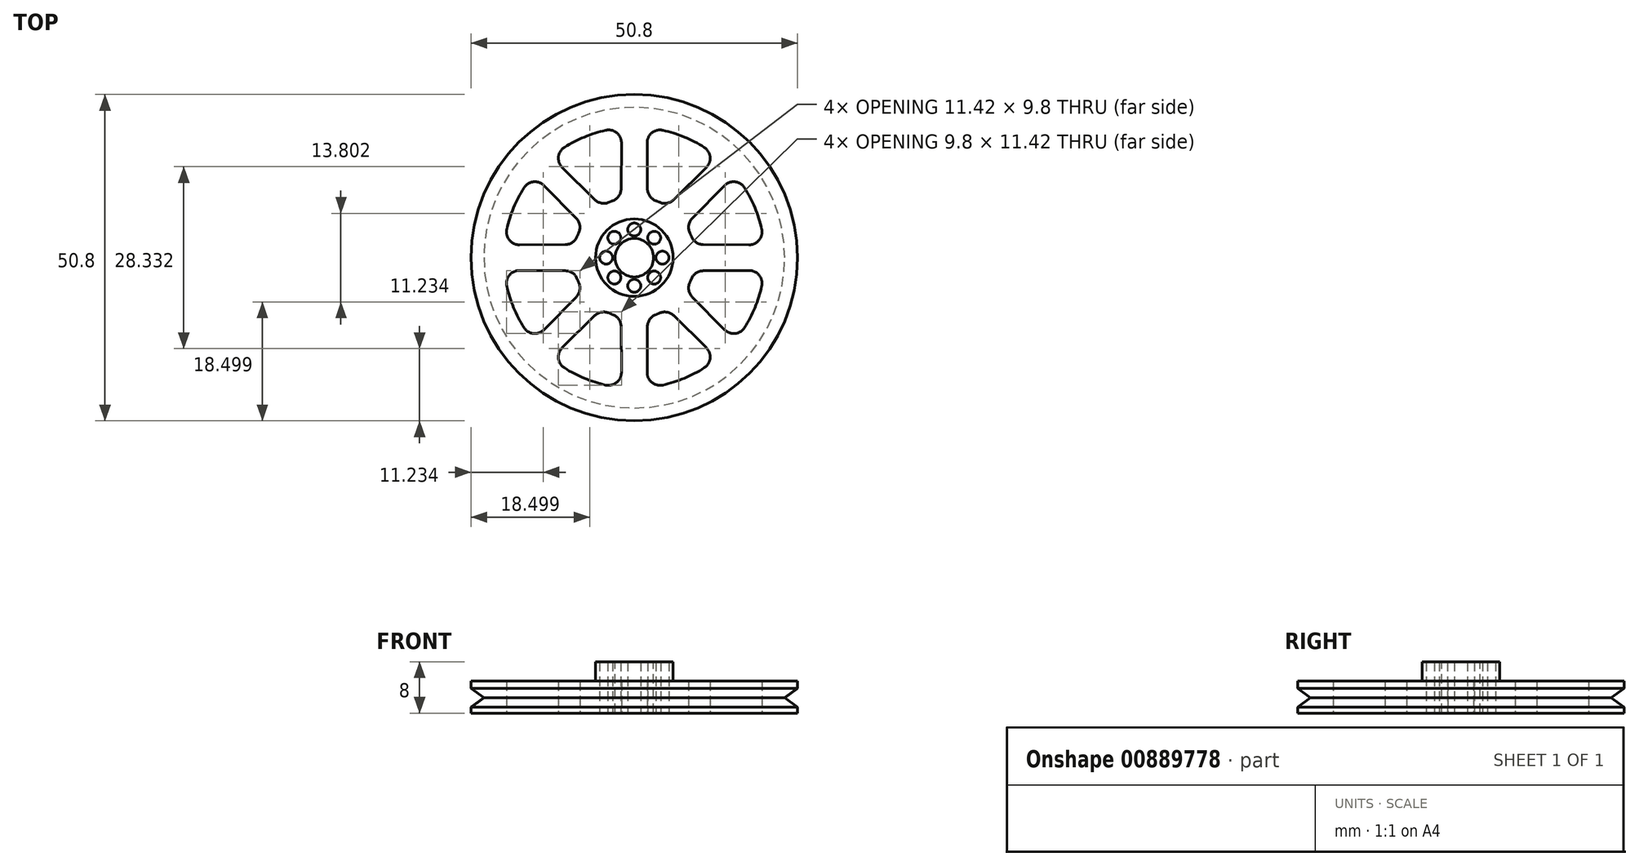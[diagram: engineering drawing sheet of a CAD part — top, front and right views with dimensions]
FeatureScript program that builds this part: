
annotation { "Feature Type Name" : "Feature", "Feature Type Description" : "" }
export const myFeature = defineFeature(function(context is Context, id is Id, definition is map)
    precondition{}
    {
        {
            var Q0;
            Q0=qCreatedBy(makeId("Top.planeOp"),FACE);
            var sketch = newSketch(context, id + "F0", { "sketchPlane" : qUnion([Q0])});
            skCircle(sketch, "E0", {"center": v(0, 0) * mm, "radius": 25.4 * mm});
            skCircle(sketch, "E1", {"center": v(0, 0) * mm, "radius": 3.12 * mm});
            skArc(sketch, "E2.0", {"start": v(-4.44, 19.83) * mm, "mid": v(-7.78, 18.77) * mm, "end": v(-10.88, 17.16) * mm});
            skArc(sketch, "E3.0", {"start": v(-3.34, 8.87) * mm, "mid": v(-3.63, 8.75) * mm, "end": v(-3.9, 8.63) * mm});
            skLineSegment(sketch, "E4.0", {"start": v(-2, 17.87) * mm, "end": v(-2.04, 10.73) * mm});
            skLineSegment(sketch, "E5.0", {"start": v(2, 17.87) * mm, "end": v(2.04, 10.73) * mm});
            skPoint(sketch, "E6.orphan", {"position": v(0, 22.85) * mm});
            skPoint(sketch, "E7.visualSharp", {"position": v(-1.99, 20.22) * mm});
            skArc(sketch, "E7.filletArc", {"start": v(-2, 17.87) * mm, "mid": v(-2.74, 19.44) * mm, "end": v(-4.44, 19.83) * mm});
            skPoint(sketch, "E8.visualSharp", {"position": v(1.99, 20.22) * mm});
            skArc(sketch, "E8.filletArc", {"start": v(4.44, 19.83) * mm, "mid": v(2.74, 19.44) * mm, "end": v(2, 17.87) * mm});
            skPoint(sketch, "E9.visualSharp", {"position": v(-2.05, 9.25) * mm});
            skArc(sketch, "E9.filletArc", {"start": v(-3.34, 8.87) * mm, "mid": v(-2.4, 9.6) * mm, "end": v(-2.04, 10.73) * mm});
            skPoint(sketch, "E10.visualSharp", {"position": v(2.05, 9.25) * mm});
            skArc(sketch, "E10.filletArc", {"start": v(2.04, 10.73) * mm, "mid": v(2.4, 9.6) * mm, "end": v(3.34, 8.87) * mm});
            skArc(sketch, "E11.1.0", {"start": v(-14.05, 11.22) * mm, "mid": v(-15.68, 11.8) * mm, "end": v(-17.16, 10.88) * mm});
            skLineSegment(sketch, "E11.1.1", {"start": v(-14.05, 11.22) * mm, "end": v(-9.03, 6.14) * mm});
            skArc(sketch, "E11.1.2", {"start": v(-8.63, 3.9) * mm, "mid": v(-8.48, 5.09) * mm, "end": v(-9.03, 6.14) * mm});
            skArc(sketch, "E11.1.3", {"start": v(-10.88, 17.16) * mm, "mid": v(-11.8, 15.68) * mm, "end": v(-11.22, 14.05) * mm});
            skLineSegment(sketch, "E11.1.4", {"start": v(-11.22, 14.05) * mm, "end": v(-6.14, 9.03) * mm});
            skArc(sketch, "E11.1.5", {"start": v(-6.14, 9.03) * mm, "mid": v(-5.09, 8.48) * mm, "end": v(-3.9, 8.63) * mm});
            skArc(sketch, "E11.2.0", {"start": v(-17.87, -2) * mm, "mid": v(-19.44, -2.74) * mm, "end": v(-19.83, -4.44) * mm});
            skLineSegment(sketch, "E11.2.1", {"start": v(-17.87, -2) * mm, "end": v(-10.73, -2.04) * mm});
            skArc(sketch, "E11.2.2", {"start": v(-8.87, -3.34) * mm, "mid": v(-9.6, -2.4) * mm, "end": v(-10.73, -2.04) * mm});
            skArc(sketch, "E11.2.3", {"start": v(-19.83, 4.44) * mm, "mid": v(-19.44, 2.74) * mm, "end": v(-17.87, 2) * mm});
            skLineSegment(sketch, "E11.2.4", {"start": v(-17.87, 2) * mm, "end": v(-10.73, 2.04) * mm});
            skArc(sketch, "E11.2.5", {"start": v(-10.73, 2.04) * mm, "mid": v(-9.6, 2.4) * mm, "end": v(-8.87, 3.34) * mm});
            skArc(sketch, "E11.3.0", {"start": v(-11.22, -14.05) * mm, "mid": v(-11.8, -15.68) * mm, "end": v(-10.88, -17.16) * mm});
            skLineSegment(sketch, "E11.3.1", {"start": v(-11.22, -14.05) * mm, "end": v(-6.14, -9.03) * mm});
            skArc(sketch, "E11.3.2", {"start": v(-3.9, -8.63) * mm, "mid": v(-5.09, -8.48) * mm, "end": v(-6.14, -9.03) * mm});
            skArc(sketch, "E11.3.3", {"start": v(-17.16, -10.88) * mm, "mid": v(-15.68, -11.8) * mm, "end": v(-14.05, -11.22) * mm});
            skLineSegment(sketch, "E11.3.4", {"start": v(-14.05, -11.22) * mm, "end": v(-9.03, -6.14) * mm});
            skArc(sketch, "E11.3.5", {"start": v(-9.03, -6.14) * mm, "mid": v(-8.48, -5.09) * mm, "end": v(-8.63, -3.9) * mm});
            skArc(sketch, "E11.4.0", {"start": v(2, -17.87) * mm, "mid": v(2.74, -19.44) * mm, "end": v(4.44, -19.83) * mm});
            skLineSegment(sketch, "E11.4.1", {"start": v(2, -17.87) * mm, "end": v(2.04, -10.73) * mm});
            skArc(sketch, "E11.4.2", {"start": v(3.34, -8.87) * mm, "mid": v(2.4, -9.6) * mm, "end": v(2.04, -10.73) * mm});
            skArc(sketch, "E11.4.3", {"start": v(-4.44, -19.83) * mm, "mid": v(-2.74, -19.44) * mm, "end": v(-2, -17.87) * mm});
            skLineSegment(sketch, "E11.4.4", {"start": v(-2, -17.87) * mm, "end": v(-2.04, -10.73) * mm});
            skArc(sketch, "E11.4.5", {"start": v(-2.04, -10.73) * mm, "mid": v(-2.4, -9.6) * mm, "end": v(-3.34, -8.87) * mm});
            skArc(sketch, "E11.5.0", {"start": v(14.05, -11.22) * mm, "mid": v(15.68, -11.8) * mm, "end": v(17.16, -10.88) * mm});
            skLineSegment(sketch, "E11.5.1", {"start": v(14.05, -11.22) * mm, "end": v(9.03, -6.14) * mm});
            skArc(sketch, "E11.5.2", {"start": v(8.63, -3.9) * mm, "mid": v(8.48, -5.09) * mm, "end": v(9.03, -6.14) * mm});
            skArc(sketch, "E11.5.3", {"start": v(10.88, -17.16) * mm, "mid": v(11.8, -15.68) * mm, "end": v(11.22, -14.05) * mm});
            skLineSegment(sketch, "E11.5.4", {"start": v(11.22, -14.05) * mm, "end": v(6.14, -9.03) * mm});
            skArc(sketch, "E11.5.5", {"start": v(6.14, -9.03) * mm, "mid": v(5.09, -8.48) * mm, "end": v(3.9, -8.63) * mm});
            skArc(sketch, "E11.6.0", {"start": v(17.87, 2) * mm, "mid": v(19.44, 2.74) * mm, "end": v(19.83, 4.44) * mm});
            skLineSegment(sketch, "E11.6.1", {"start": v(17.87, 2) * mm, "end": v(10.73, 2.04) * mm});
            skArc(sketch, "E11.6.2", {"start": v(8.87, 3.34) * mm, "mid": v(9.6, 2.4) * mm, "end": v(10.73, 2.04) * mm});
            skArc(sketch, "E11.6.3", {"start": v(19.83, -4.44) * mm, "mid": v(19.44, -2.74) * mm, "end": v(17.87, -2) * mm});
            skLineSegment(sketch, "E11.6.4", {"start": v(17.87, -2) * mm, "end": v(10.73, -2.04) * mm});
            skArc(sketch, "E11.6.5", {"start": v(10.73, -2.04) * mm, "mid": v(9.6, -2.4) * mm, "end": v(8.87, -3.34) * mm});
            skArc(sketch, "E11.7.0", {"start": v(11.22, 14.05) * mm, "mid": v(11.8, 15.68) * mm, "end": v(10.88, 17.16) * mm});
            skLineSegment(sketch, "E11.7.1", {"start": v(11.22, 14.05) * mm, "end": v(6.14, 9.03) * mm});
            skArc(sketch, "E11.7.2", {"start": v(3.9, 8.63) * mm, "mid": v(5.09, 8.48) * mm, "end": v(6.14, 9.03) * mm});
            skArc(sketch, "E11.7.3", {"start": v(17.16, 10.88) * mm, "mid": v(15.68, 11.8) * mm, "end": v(14.05, 11.22) * mm});
            skLineSegment(sketch, "E11.7.4", {"start": v(14.05, 11.22) * mm, "end": v(9.03, 6.14) * mm});
            skArc(sketch, "E11.7.5", {"start": v(9.03, 6.14) * mm, "mid": v(8.48, 5.09) * mm, "end": v(8.63, 3.9) * mm});
            skArc(sketch, "E12.trimOffspring", {"start": v(-17.16, 10.88) * mm, "mid": v(-18.77, 7.78) * mm, "end": v(-19.83, 4.44) * mm});
            skArc(sketch, "E13.trimOffspring", {"start": v(-8.63, 3.9) * mm, "mid": v(-8.75, 3.63) * mm, "end": v(-8.87, 3.34) * mm});
            skArc(sketch, "E14.trimOffspring", {"start": v(-8.87, -3.34) * mm, "mid": v(-8.75, -3.63) * mm, "end": v(-8.63, -3.9) * mm});
            skArc(sketch, "E15.trimOffspring", {"start": v(-19.83, -4.44) * mm, "mid": v(-18.77, -7.78) * mm, "end": v(-17.16, -10.88) * mm});
            skArc(sketch, "E16.trimOffspring", {"start": v(-10.88, -17.16) * mm, "mid": v(-7.78, -18.77) * mm, "end": v(-4.44, -19.83) * mm});
            skArc(sketch, "E17.trimOffspring", {"start": v(-3.9, -8.63) * mm, "mid": v(-3.63, -8.75) * mm, "end": v(-3.34, -8.87) * mm});
            skArc(sketch, "E18.trimOffspring", {"start": v(3.34, -8.87) * mm, "mid": v(3.63, -8.75) * mm, "end": v(3.9, -8.63) * mm});
            skArc(sketch, "E19.trimOffspring", {"start": v(8.63, -3.9) * mm, "mid": v(8.75, -3.63) * mm, "end": v(8.87, -3.34) * mm});
            skArc(sketch, "E20.trimOffspring", {"start": v(8.87, 3.34) * mm, "mid": v(8.75, 3.63) * mm, "end": v(8.63, 3.9) * mm});
            skArc(sketch, "E21.trimOffspring", {"start": v(3.9, 8.63) * mm, "mid": v(3.63, 8.75) * mm, "end": v(3.34, 8.87) * mm});
            skArc(sketch, "E22.trimOffspring", {"start": v(10.88, 17.16) * mm, "mid": v(7.78, 18.77) * mm, "end": v(4.44, 19.83) * mm});
            skArc(sketch, "E23.trimOffspring", {"start": v(19.83, 4.44) * mm, "mid": v(18.77, 7.78) * mm, "end": v(17.16, 10.88) * mm});
            skArc(sketch, "E24.trimOffspring", {"start": v(17.16, -10.88) * mm, "mid": v(18.77, -7.78) * mm, "end": v(19.83, -4.44) * mm});
            skArc(sketch, "E25.trimOffspring", {"start": v(4.44, -19.83) * mm, "mid": v(7.78, -18.77) * mm, "end": v(10.88, -17.16) * mm});
            skSolve(sketch);
        }
        {
            var Q0;
            Q0=makeQuery(id+"F0.imprint","IMPRINT",FACE,{"disambiguationData":[TD([[makeQuery(id+"F0.imprint","IMPRINT",EDGE,{"derivedFrom":sQuery(id+"F0.wireOp",EDGE,"E0")}),1.0]])]});
            extrude(context, id + "F1", {"entities" : qUnion([Q0]), "depth" : 5 * mm, "offsetDistance" : 25.4 * mm});
        }
        {
            var Q0;
            Q0=qCreatedBy(makeId("Top.planeOp"),FACE);
            var sketch = newSketch(context, id + "F2", { "sketchPlane" : qUnion([Q0])});
            skCircle(sketch, "E26", {"center": v(0, 0) * mm, "radius": 6.03 * mm});
            skSolve(sketch);
        }
        {
            var Q0;
            Q0=makeQuery(id+"F2.imprint","IMPRINT",FACE,{"disambiguationData":[TD([[makeQuery(id+"F2.imprint","IMPRINT",EDGE,{"derivedFrom":sQuery(id+"F2.wireOp",EDGE,"E26")}),1.0]])]});
            extrude(context, id + "F3", {"entities" : qUnion([Q0]), "operationType" : NewBodyOperationType.ADD, "depth" : 8 * mm, "offsetDistance" : 25.4 * mm});
        }
        {
            var Q0;
            Q0=makeQuery(id+"F3.opExtrude","CAP_FACE",FACE,{"disambiguationData":[OSD([sQuery(id+"F2.wireOp",EDGE,"E26")])],"isStart":false});
            var sketch = newSketch(context, id + "F4", { "sketchPlane" : qUnion([Q0])});
            skCircle(sketch, "E27", {"center": v(0, 0) * mm, "radius": 3 * mm});
            skSolve(sketch);
        }
        {
            var Q0;
            Q0=makeQuery(id+"F4.imprint","IMPRINT",FACE,{"disambiguationData":[TD([[makeQuery(id+"F4.imprint","IMPRINT",EDGE,{"derivedFrom":sQuery(id+"F4.wireOp",EDGE,"E27")}),1.0]])]});
            extrude(context, id + "F5", {"entities" : qUnion([Q0]), "operationType" : NewBodyOperationType.REMOVE, "endBound" : BoundingType.THROUGH_ALL, "oppositeDirection" : true, "depth" : 25.4 * mm, "offsetDistance" : 25.4 * mm});
        }
        {
            var Q0;
            Q0=qCreatedBy(makeId("Right.planeOp"),FACE);
            var sketch = newSketch(context, id + "F6", { "sketchPlane" : qUnion([Q0])});
            skLineSegment(sketch, "E28", {"start": v(25.4, 2.4) * mm, "end": v(23.4, 2.4) * mm});
            skLineSegment(sketch, "E29", {"start": v(23.4, 2.4) * mm, "end": v(25.46, 3.9) * mm});
            skLineSegment(sketch, "E30", {"start": v(25.46, 3.9) * mm, "end": v(25.4, 2.4) * mm});
            skLineSegment(sketch, "E31.MirrorCS", {"start": v(23.4, 2.4) * mm, "end": v(25.46, 0.9) * mm});
            skLineSegment(sketch, "E32.MirrorCS", {"start": v(25.46, 0.9) * mm, "end": v(25.4, 2.4) * mm});
            skLineSegment(sketch, "E33", {"start": v(0, 19.4) * mm, "end": v(0, -3.2) * mm, "construction": true});
            skSolve(sketch);
        }
        {
            var Q0;
            Q0=qSketchRegion(id+"F6",true);
            var Q1;
            Q1=sQuery(id+"F6.wireOp",EDGE,"E33");
            revolve(context, id + "F7", {"operationType" : NewBodyOperationType.REMOVE, "surfaceOperationType" : NewSurfaceOperationType.NEW, "entities" : qUnion([Q0]), "axis" : qUnion([Q1]), "revolveType" : RevolveType.FULL, "oppositeDirection" : true});
        }
        {
            var Q0;
            Q0=qCreatedBy(makeId("Top.planeOp"),FACE);
            var sketch = newSketch(context, id + "F8", { "sketchPlane" : qUnion([Q0])});
            skCircle(sketch, "E34", {"center": v(0, 4.38) * mm, "radius": 1 * mm});
            skCircle(sketch, "E35.1.0", {"center": v(-3.1, 3.1) * mm, "radius": 1 * mm});
            skCircle(sketch, "E35.2.0", {"center": v(-4.38, 0) * mm, "radius": 1 * mm});
            skPoint(sketch, "E35.center", {"position": v(0, 0) * mm});
            skCircle(sketch, "E36.1.3.0", {"center": v(-3.1, -3.1) * mm, "radius": 1 * mm});
            skCircle(sketch, "E36.1.4.0", {"center": v(0, -4.38) * mm, "radius": 1 * mm});
            skCircle(sketch, "E36.1.5.0", {"center": v(3.1, -3.1) * mm, "radius": 1 * mm});
            skCircle(sketch, "E36.1.6.0", {"center": v(4.38, 0) * mm, "radius": 1 * mm});
            skCircle(sketch, "E36.1.7.0", {"center": v(3.1, 3.1) * mm, "radius": 1 * mm});
            skSolve(sketch);
        }
        {
            var Q0;
            Q0 = qSketchRegion(id + "F8", true);
            extrude(context, id + "F9", {"entities" : qUnion([Q0]), "operationType" : NewBodyOperationType.REMOVE, "endBound" : BoundingType.THROUGH_ALL, "depth" : 25.4 * mm, "offsetDistance" : 25.4 * mm});
        }
    });
